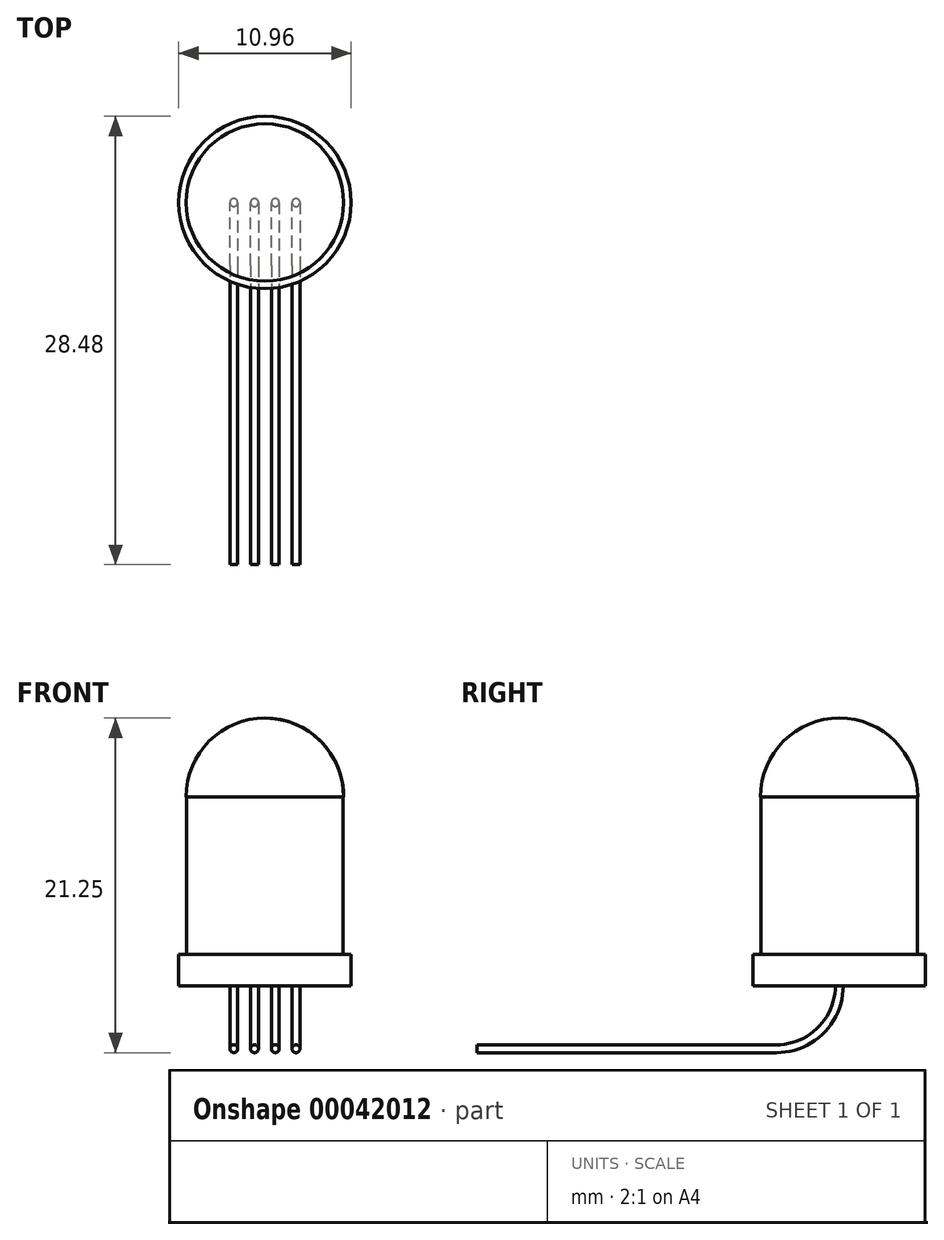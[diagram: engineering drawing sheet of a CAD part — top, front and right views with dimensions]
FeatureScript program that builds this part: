
annotation { "Feature Type Name" : "Feature", "Feature Type Description" : "" }
export const myFeature = defineFeature(function(context is Context, id is Id, definition is map)
    precondition{}
    {
        {
            var Q0;
            Q0=qCreatedBy(makeId("Top.planeOp"),FACE);
            var sketch = newSketch(context, id + "F0", { "sketchPlane" : qUnion([Q0])});
            skCircle(sketch, "E0", {"center": v(0, 0) * mm, "radius": 5.47 * mm});
            skSolve(sketch);
        }
        {
            var Q0;
            Q0=qSketchRegion(id+"F0",true);
            extrude(context, id + "F1", {"entities" : qUnion([Q0]), "depth" : 2 * mm});
        }
        {
            var Q0;
            Q0=makeQuery(id+"F1.opExtrude","CAP_FACE",FACE,{"disambiguationData":[OSD([sQuery(id+"F0.wireOp",EDGE,"E0")])],"isStart":false});
            var sketch = newSketch(context, id + "F2", { "sketchPlane" : qUnion([Q0])});
            skCircle(sketch, "E1", {"center": v(0, 0) * mm, "radius": 4.97 * mm});
            skSolve(sketch);
        }
        {
            var Q0;
            Q0=qSketchRegion(id+"F2",true);
            extrude(context, id + "F3", {"entities" : qUnion([Q0]), "operationType" : NewBodyOperationType.ADD, "depth" : 10 * mm});
        }
        {
            var Q0;
            Q0=qCreatedBy(makeId("Front.planeOp"),FACE);
            var sketch = newSketch(context, id + "F4", { "sketchPlane" : qUnion([Q0])});
            skLineSegment(sketch, "E2", {"start": v(0, 12) * mm, "end": v(5, 12) * mm});
            skLineSegment(sketch, "E3", {"start": v(0, 12) * mm, "end": v(0, 17) * mm});
            skArc(sketch, "E4", {"start": v(5, 12) * mm, "mid": v(3.54, 15.54) * mm, "end": v(0, 17) * mm});
            skSolve(sketch);
        }
        {
            var Q0;
            Q0=makeQuery(id+"F4.imprint","IMPRINT",FACE,{"disambiguationData":[TD([[makeQuery(id+"F4.imprint","IMPRINT",EDGE,{"derivedFrom":sQuery(id+"F4.wireOp",EDGE,"E2")}),1.0]])]});
            var Q1;
            Q1=sQuery(id+"F4.wireOp",EDGE,"E3");
            revolve(context, id + "F5", {"operationType" : NewBodyOperationType.ADD, "entities" : qUnion([Q0]), "axis" : qUnion([Q1]), "revolveType" : RevolveType.FULL});
        }
        {
            var Q0;
            Q0=qCreatedBy(makeId("Top.planeOp"),FACE);
            var sketch = newSketch(context, id + "F6", { "sketchPlane" : qUnion([Q0])});
            skCircle(sketch, "E5", {"center": v(-1.97, 0) * mm, "radius": 0.25 * mm});
            skCircle(sketch, "E6", {"center": v(1.97, 0) * mm, "radius": 0.25 * mm});
            skCircle(sketch, "E7", {"center": v(-0.66, 0) * mm, "radius": 0.25 * mm});
            skCircle(sketch, "E8", {"center": v(0.66, 0) * mm, "radius": 0.25 * mm});
            skSolve(sketch);
        }
        {
            var Q0;
            Q0=qCreatedBy(makeId("Right.planeOp"),FACE);
            cPlane(context, id + "F7", {"entities" : qUnion([Q0]), "cplaneType" : CPlaneType.OFFSET, "offset" : 1.97 * mm, "width" : 150 * mm, "height" : 150 * mm});
        }
        {
            var Q0;
            Q0=qCreatedBy(id+"F7.planeOp",FACE);
            var sketch = newSketch(context, id + "F8", { "sketchPlane" : qUnion([Q0])});
            skLineSegment(sketch, "E9", {"start": v(-4, -4) * mm, "end": v(-23, -4) * mm});
            skPoint(sketch, "E10", {"position": v(-4, -4) * mm});
            skArc(sketch, "E11", {"start": v(-4, -4) * mm, "mid": v(-1.17, -2.83) * mm, "end": v(0, 0) * mm});
            skSolve(sketch);
        }
        {
            var Q0;
            Q0=qSketchRegion(id+"F6",true);
            var Q1;
            Q1=qConstructionFilter(qBodyType(qCreatedBy(id+"F8",EDGE),BodyType.WIRE),ConstructionObject.NO);
            sweep(context, id + "F9", {"operationType" : NewBodyOperationType.ADD, "profiles" : qUnion([Q0]), "path" : qUnion([Q1])});
        }
    });
